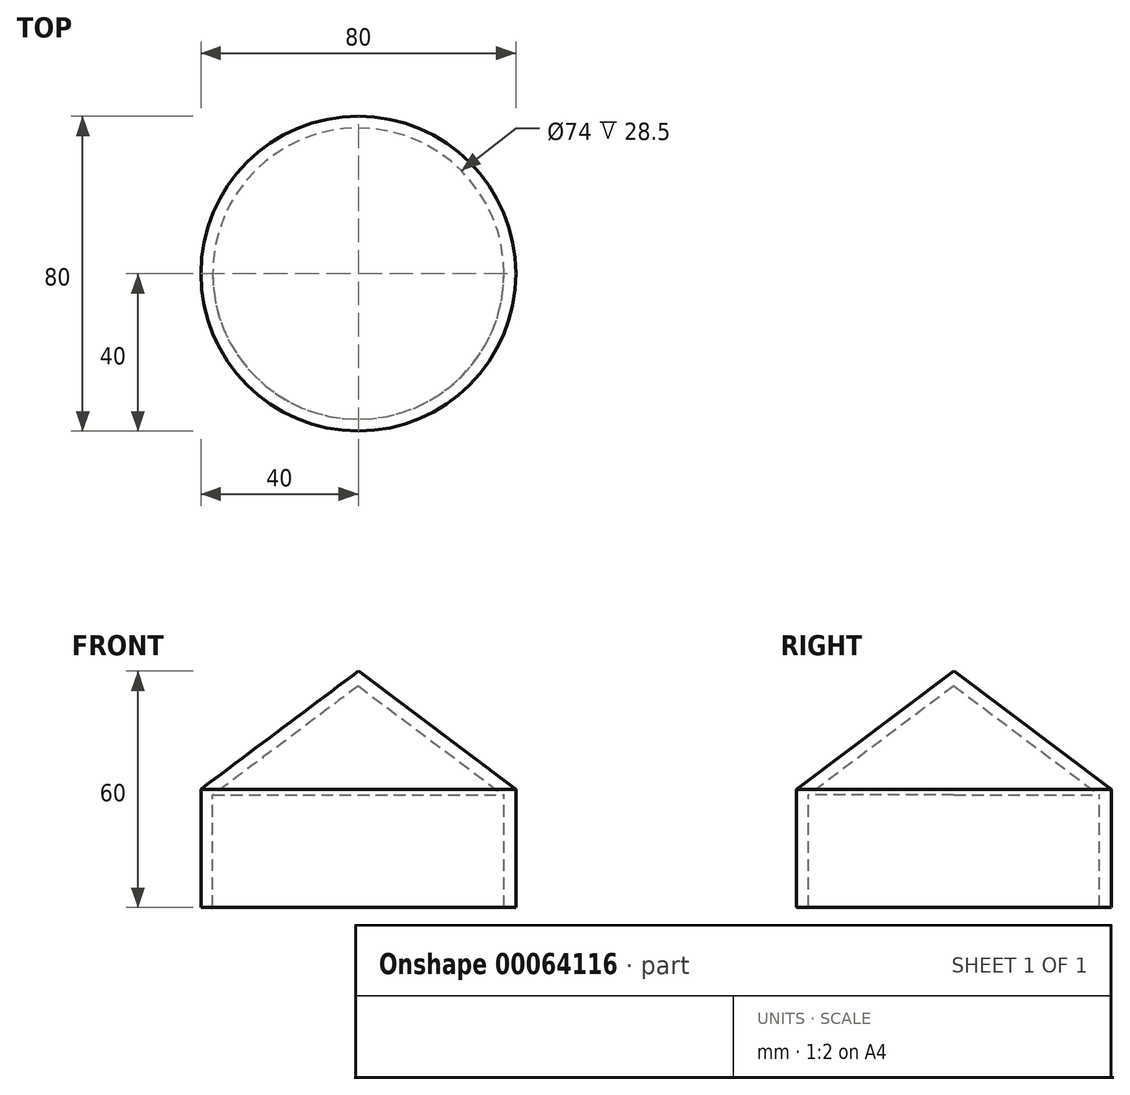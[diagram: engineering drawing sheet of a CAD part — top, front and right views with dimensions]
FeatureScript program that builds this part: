
annotation { "Feature Type Name" : "Feature", "Feature Type Description" : "" }
export const myFeature = defineFeature(function(context is Context, id is Id, definition is map)
    precondition{}
    {
        {
            var Q0;
            Q0=qCreatedBy(makeId("Right.planeOp"),FACE);
            var sketch = newSketch(context, id + "F0", { "sketchPlane" : qUnion([Q0])});
            skLineSegment(sketch, "E0", {"start": v(0, 0) * mm, "end": v(-40, 0) * mm});
            skLineSegment(sketch, "E1", {"start": v(-40, 0) * mm, "end": v(-40, 30) * mm});
            skLineSegment(sketch, "E2", {"start": v(-40, 30) * mm, "end": v(0, 60) * mm});
            skLineSegment(sketch, "E3", {"start": v(0, 60) * mm, "end": v(0, 0) * mm});
            skSolve(sketch);
        }
        {
            var Q0;
            Q0=makeQuery(id+"F0.imprint","IMPRINT",FACE,{"disambiguationData":[TD([[makeQuery(id+"F0.imprint","IMPRINT",EDGE,{"derivedFrom":sQuery(id+"F0.wireOp",EDGE,"E0")}),-1.0]])]});
            var Q1;
            Q1=sQuery(id+"F0.wireOp",EDGE,"E3");
            revolve(context, id + "F1", {"entities" : qUnion([Q0]), "axis" : qUnion([Q1]), "revolveType" : RevolveType.FULL});
        }
        {
            var Q0;
            Q0=makeQuery(id+"F1.opRevolve","SWEPT_FACE",FACE,{"disambiguationData":[OSD([sQuery(id+"F0.wireOp",EDGE,"E0")])]});
            shell(context, id + "F2", {"entities" : qUnion([Q0]), "thickness" : 3 * mm});
        }
    });
